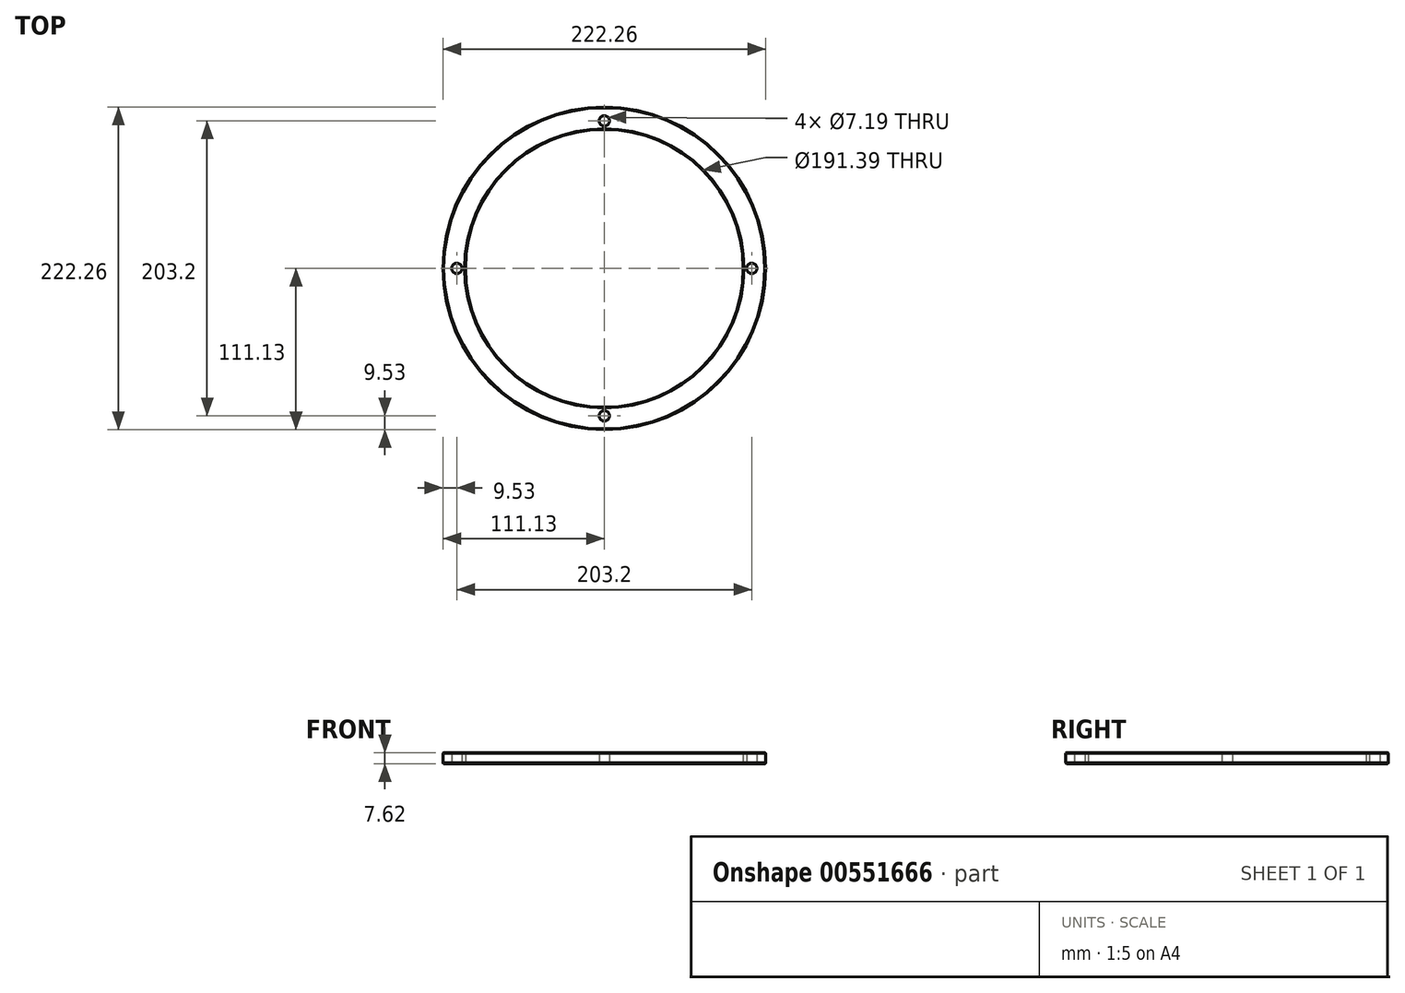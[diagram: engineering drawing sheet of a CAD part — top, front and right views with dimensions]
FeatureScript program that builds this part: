
annotation { "Feature Type Name" : "Feature", "Feature Type Description" : "" }
export const myFeature = defineFeature(function(context is Context, id is Id, definition is map)
    precondition{}
    {
        {
            var Q0;
            Q0=qCreatedBy(makeId("Top.planeOp"),FACE);
            var sketch = newSketch(context, id + "F0", { "sketchPlane" : qUnion([Q0])});
            skCircle(sketch, "E0", {"center": v(0, 0) * mm, "radius": 111.13 * mm});
            skCircle(sketch, "E1", {"center": v(0, 0) * mm, "radius": 95.7 * mm});
            skSolve(sketch);
        }
        {
            var Q0;
            Q0=makeQuery(id+"F0.imprint","IMPRINT",FACE,{"disambiguationData":[TD([[makeQuery(id+"F0.imprint","IMPRINT",EDGE,{"derivedFrom":sQuery(id+"F0.wireOp",EDGE,"E0")}),1.0]])]});
            extrude(context, id + "F1", {"entities" : qUnion([Q0]), "depth" : 7.62 * mm, "offsetDistance" : 25.4 * mm});
        }
        {
            var Q0;
            Q0=qCreatedBy(makeId("Top.planeOp"),FACE);
            var sketch = newSketch(context, id + "F2", { "sketchPlane" : qUnion([Q0])});
            skCircle(sketch, "E2", {"center": v(0, 0) * mm, "radius": 101.6 * mm});
            skLineSegment(sketch, "E3", {"start": v(0, 101.6) * mm, "end": v(0, -101.6) * mm});
            skCircle(sketch, "E4", {"center": v(-101.6, 0) * mm, "radius": 3.57 * mm});
            skLineSegment(sketch, "E5", {"start": v(101.6, 0) * mm, "end": v(-101.6, 0) * mm});
            skSolve(sketch);
        }
        {
            var Q0;
            Q0=sQuery(id+"F2.wireOp",VERTEX,"E4.center");
            var Q1;
            Q1=sQuery(id+"F2.wireOp",VERTEX,"E3.start");
            var Q2;
            Q2=sQuery(id+"F2.wireOp",VERTEX,"E5.start");
            var Q3;
            Q3=sQuery(id+"F2.wireOp",VERTEX,"E3.end");
            var Q4;
            Q4=makeQuery(id+"F1.opExtrude","SWEPT_BODY",BODY,{"disambiguationData":[OSD([sQuery(id+"F0.wireOp",EDGE,"E0"),sQuery(id+"F0.wireOp",EDGE,"E1")])]});
            hole(context, id + "F3", {"style" : HoleStyle.SIMPLE, "endStyle" : HoleEndStyle.THROUGH, "oppositeDirection" : true, "holeDiameter" : 7.2 * mm, "isTappedThrough" : true, "tappedDepth" : 12.7 * mm, "tapClearance" : 3, "locations" : qUnion([Q0, Q1, Q2, Q3]), "scope" : qUnion([Q4])});
        }
        {
            var Q0;
            Q0=makeQuery(id+"F1.opExtrude","CAP_EDGE",EDGE,{"disambiguationData":[OSD([sQuery(id+"F0.wireOp",EDGE,"E0")])],"isStart":false});
            var Q1;
            Q1=makeQuery(id+"F1.opExtrude","CAP_EDGE",EDGE,{"disambiguationData":[OSD([sQuery(id+"F0.wireOp",EDGE,"E1")])],"isStart":true});
            var Q2;
            Q2=makeQuery(id+"F1.opExtrude","CAP_EDGE",EDGE,{"disambiguationData":[OSD([sQuery(id+"F0.wireOp",EDGE,"E1")])],"isStart":false});
            var Q3;
            Q3=makeQuery(id+"F3.hole-1.boolean.opBoolean","INTERSECT",EDGE,{"derivedFrom":[makeQuery(id+"F1.opExtrude","CAP_FACE",FACE,{"disambiguationData":[OSD([sQuery(id+"F0.wireOp",EDGE,"E0"),sQuery(id+"F0.wireOp",EDGE,"E1")])],"isStart":false}),makeQuery(id+"F3.hole-1.opRevolve","SWEPT_FACE",FACE,{"disambiguationData":[OSD([sQuery(id+"F3.hole-1.sketch.wireOp",EDGE,"core_line_2")])]})]});
            var Q4;
            Q4=makeQuery(id+"F3.hole-0.boolean.opBoolean","INTERSECT",EDGE,{"derivedFrom":[makeQuery(id+"F1.opExtrude","CAP_FACE",FACE,{"disambiguationData":[OSD([sQuery(id+"F0.wireOp",EDGE,"E0"),sQuery(id+"F0.wireOp",EDGE,"E1")])],"isStart":false}),makeQuery(id+"F3.hole-0.opRevolve","SWEPT_FACE",FACE,{"disambiguationData":[OSD([sQuery(id+"F3.hole-0.sketch.wireOp",EDGE,"core_line_2")])]})]});
            var Q5;
            Q5=makeQuery(id+"F3.hole-3.boolean.opBoolean","INTERSECT",EDGE,{"derivedFrom":[makeQuery(id+"F1.opExtrude","CAP_FACE",FACE,{"disambiguationData":[OSD([sQuery(id+"F0.wireOp",EDGE,"E0"),sQuery(id+"F0.wireOp",EDGE,"E1")])],"isStart":false}),makeQuery(id+"F3.hole-3.opRevolve","SWEPT_FACE",FACE,{"disambiguationData":[OSD([sQuery(id+"F3.hole-3.sketch.wireOp",EDGE,"core_line_2")])]})]});
            var Q6;
            Q6=makeQuery(id+"F3.hole-2.boolean.opBoolean","INTERSECT",EDGE,{"derivedFrom":[makeQuery(id+"F1.opExtrude","CAP_FACE",FACE,{"disambiguationData":[OSD([sQuery(id+"F0.wireOp",EDGE,"E0"),sQuery(id+"F0.wireOp",EDGE,"E1")])],"isStart":false}),makeQuery(id+"F3.hole-2.opRevolve","SWEPT_FACE",FACE,{"disambiguationData":[OSD([sQuery(id+"F3.hole-2.sketch.wireOp",EDGE,"core_line_2")])]})]});
            var Q7;
            Q7=makeQuery(id+"F1.opExtrude","CAP_EDGE",EDGE,{"disambiguationData":[OSD([sQuery(id+"F0.wireOp",EDGE,"E0")])],"isStart":true});
            var Q8;
            Q8=makeQuery(id+"F3.hole-1.boolean.opBoolean","COPY",EDGE,{"derivedFrom":makeQuery(id+"F3.hole-1.opRevolve","SWEPT_EDGE",EDGE,{"disambiguationData":[OSD([sQuery(id+"F3.hole-1.sketch.wireOp",EDGE,"core_line_2"),sQuery(id+"F3.hole-1.sketch.wireOp",EDGE,"core_line_3")])]})});
            var Q9;
            Q9=makeQuery(id+"F3.hole-3.boolean.opBoolean","COPY",EDGE,{"derivedFrom":makeQuery(id+"F3.hole-3.opRevolve","SWEPT_EDGE",EDGE,{"disambiguationData":[OSD([sQuery(id+"F3.hole-3.sketch.wireOp",EDGE,"core_line_2"),sQuery(id+"F3.hole-3.sketch.wireOp",EDGE,"core_line_3")])]})});
            var Q10;
            Q10=makeQuery(id+"F3.hole-2.boolean.opBoolean","COPY",EDGE,{"derivedFrom":makeQuery(id+"F3.hole-2.opRevolve","SWEPT_EDGE",EDGE,{"disambiguationData":[OSD([sQuery(id+"F3.hole-2.sketch.wireOp",EDGE,"core_line_2"),sQuery(id+"F3.hole-2.sketch.wireOp",EDGE,"core_line_3")])]})});
            var Q11;
            Q11=makeQuery(id+"F3.hole-0.boolean.opBoolean","COPY",EDGE,{"derivedFrom":makeQuery(id+"F3.hole-0.opRevolve","SWEPT_EDGE",EDGE,{"disambiguationData":[OSD([sQuery(id+"F3.hole-0.sketch.wireOp",EDGE,"core_line_2"),sQuery(id+"F3.hole-0.sketch.wireOp",EDGE,"core_line_3")])]})});
            chamfer(context, id + "F4", {"entities" : qUnion([Q0, Q1, Q2, Q3, Q4, Q5, Q6, Q7, Q8, Q9, Q10, Q11]), "width" : 0.5 * mm, "tangentPropagation" : true});
        }
    });
